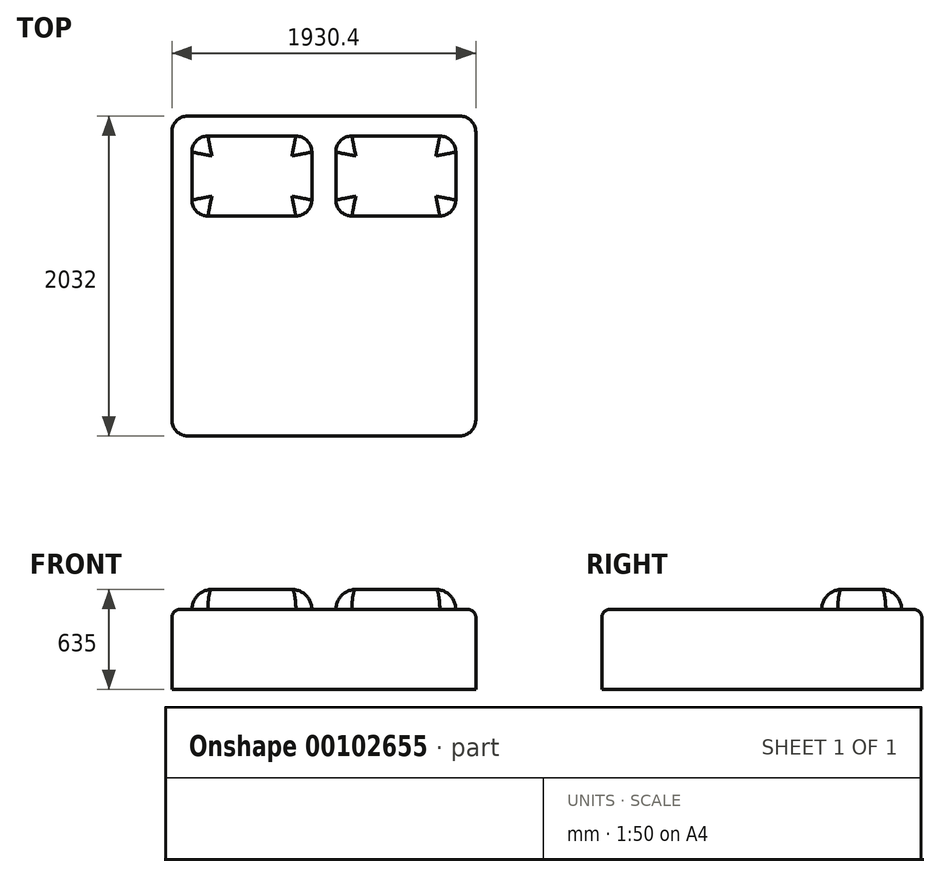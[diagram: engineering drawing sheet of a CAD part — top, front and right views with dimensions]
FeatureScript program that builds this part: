
annotation { "Feature Type Name" : "Feature", "Feature Type Description" : "" }
export const myFeature = defineFeature(function(context is Context, id is Id, definition is map)
    precondition{}
    {
        {
            var Q0;
            Q0=qCreatedBy(makeId("Top.planeOp"),FACE);
            var sketch = newSketch(context, id + "F0", { "sketchPlane" : qUnion([Q0])});
            skLineSegment(sketch, "E0.bottom", {"start": v(0, 0) * mm, "end": v(1930.4, 0) * mm});
            skLineSegment(sketch, "E0.top", {"start": v(0, 2032) * mm, "end": v(1930.4, 2032) * mm});
            skLineSegment(sketch, "E0.left", {"start": v(0, 0) * mm, "end": v(0, 2032) * mm});
            skLineSegment(sketch, "E0.right", {"start": v(1930.4, 0) * mm, "end": v(1930.4, 2032) * mm});
            skSolve(sketch);
        }
        {
            var Q0;
            Q0 = qSketchRegion(id + "F0", true);
            extrude(context, id + "F1", {"entities" : qUnion([Q0]), "depth" : 508 * mm});
        }
        {
            var Q0;
            Q0=makeQuery(id+"F1.opExtrude","CAP_FACE",FACE,{"disambiguationData":[OSD([sQuery(id+"F0.wireOp",EDGE,"E0.bottom"),sQuery(id+"F0.wireOp",EDGE,"E0.top"),sQuery(id+"F0.wireOp",EDGE,"E0.left"),sQuery(id+"F0.wireOp",EDGE,"E0.right")])],"isStart":false});
            var sketch = newSketch(context, id + "F2", { "sketchPlane" : qUnion([Q0])});
            skLineSegment(sketch, "E1.bottom", {"start": v(127, 1905) * mm, "end": v(889, 1905) * mm});
            skLineSegment(sketch, "E1.top", {"start": v(127, 1397) * mm, "end": v(889, 1397) * mm});
            skLineSegment(sketch, "E1.left", {"start": v(127, 1905) * mm, "end": v(127, 1397) * mm});
            skLineSegment(sketch, "E1.right", {"start": v(889, 1905) * mm, "end": v(889, 1397) * mm});
            skLineSegment(sketch, "E2.bottom", {"start": v(1041.4, 1905) * mm, "end": v(1803.4, 1905) * mm});
            skLineSegment(sketch, "E2.top", {"start": v(1041.4, 1397) * mm, "end": v(1803.4, 1397) * mm});
            skLineSegment(sketch, "E2.left", {"start": v(1041.4, 1905) * mm, "end": v(1041.4, 1397) * mm});
            skLineSegment(sketch, "E2.right", {"start": v(1803.4, 1905) * mm, "end": v(1803.4, 1397) * mm});
            skSolve(sketch);
        }
        {
            var Q0;
            Q0 = qSketchRegion(id + "F2", true);
            extrude(context, id + "F3", {"entities" : qUnion([Q0]), "operationType" : NewBodyOperationType.ADD, "depth" : 127 * mm});
        }
        {
            var Q0;
            Q0=makeQuery(id+"F1.opExtrude","SWEPT_EDGE",EDGE,{"disambiguationData":[OSD([sQuery(id+"F0.wireOp",EDGE,"E0.bottom"),sQuery(id+"F0.wireOp",EDGE,"E0.left")])]});
            var Q1;
            Q1=makeQuery(id+"F1.opExtrude","SWEPT_EDGE",EDGE,{"disambiguationData":[OSD([sQuery(id+"F0.wireOp",EDGE,"E0.bottom"),sQuery(id+"F0.wireOp",EDGE,"E0.right")])]});
            var Q2;
            Q2=makeQuery(id+"F1.opExtrude","SWEPT_EDGE",EDGE,{"disambiguationData":[OSD([sQuery(id+"F0.wireOp",EDGE,"E0.top"),sQuery(id+"F0.wireOp",EDGE,"E0.right")])]});
            var Q3;
            Q3=makeQuery(id+"F3.opExtrude","SWEPT_EDGE",EDGE,{"disambiguationData":[OSD([sQuery(id+"F2.wireOp",EDGE,"E2.bottom"),sQuery(id+"F2.wireOp",EDGE,"E2.right")])]});
            var Q4;
            Q4=makeQuery(id+"F3.opExtrude","SWEPT_EDGE",EDGE,{"disambiguationData":[OSD([sQuery(id+"F2.wireOp",EDGE,"E2.top"),sQuery(id+"F2.wireOp",EDGE,"E2.right")])]});
            var Q5;
            Q5=makeQuery(id+"F3.opExtrude","SWEPT_EDGE",EDGE,{"disambiguationData":[OSD([sQuery(id+"F2.wireOp",EDGE,"E2.top"),sQuery(id+"F2.wireOp",EDGE,"E2.left")])]});
            var Q6;
            Q6=makeQuery(id+"F3.opExtrude","SWEPT_EDGE",EDGE,{"disambiguationData":[OSD([sQuery(id+"F2.wireOp",EDGE,"E1.top"),sQuery(id+"F2.wireOp",EDGE,"E1.right")])]});
            var Q7;
            Q7=makeQuery(id+"F3.opExtrude","SWEPT_EDGE",EDGE,{"disambiguationData":[OSD([sQuery(id+"F2.wireOp",EDGE,"E1.bottom"),sQuery(id+"F2.wireOp",EDGE,"E1.right")])]});
            var Q8;
            Q8=makeQuery(id+"F3.opExtrude","SWEPT_EDGE",EDGE,{"disambiguationData":[OSD([sQuery(id+"F2.wireOp",EDGE,"E1.top"),sQuery(id+"F2.wireOp",EDGE,"E1.left")])]});
            var Q9;
            Q9=makeQuery(id+"F1.opExtrude","SWEPT_EDGE",EDGE,{"disambiguationData":[OSD([sQuery(id+"F0.wireOp",EDGE,"E0.top"),sQuery(id+"F0.wireOp",EDGE,"E0.left")])]});
            var Q10;
            Q10=makeQuery(id+"F3.opExtrude","SWEPT_EDGE",EDGE,{"disambiguationData":[OSD([sQuery(id+"F2.wireOp",EDGE,"E1.bottom"),sQuery(id+"F2.wireOp",EDGE,"E1.left")])]});
            var Q11;
            Q11=makeQuery(id+"F3.opExtrude","SWEPT_EDGE",EDGE,{"disambiguationData":[OSD([sQuery(id+"F2.wireOp",EDGE,"E2.bottom"),sQuery(id+"F2.wireOp",EDGE,"E2.left")])]});
            fillet(context, id + "F4", {"entities" : qUnion([Q0, Q1, Q2, Q3, Q4, Q5, Q6, Q7, Q8, Q9, Q10, Q11]), "radius" : 101.6 * mm, "tangentPropagation" : true, "allowEdgeOverflow" : false});
        }
        {
            var Q0;
            Q0=makeQuery(id+"F1.opExtrude","CAP_EDGE",EDGE,{"disambiguationData":[OSD([sQuery(id+"F0.wireOp",EDGE,"E0.left")])],"isStart":false});
            var Q1;
            {var subQ0=sQuery(id+"F0.wireOp",EDGE,"E0.left");var subQ1=sQuery(id+"F0.wireOp",EDGE,"E0.top");Q1=makeQuery(id+"F4.opFillet","BLEND_EDGE",EDGE,{"blendedFrom":[makeQuery(id+"F1.opExtrude","SWEPT_EDGE",EDGE,{"disambiguationData":[OSD([subQ1,subQ0])]}),makeQuery(id+"F1.opExtrude","CAP_FACE",FACE,{"disambiguationData":[OSD([sQuery(id+"F0.wireOp",EDGE,"E0.bottom"),subQ1,subQ0,sQuery(id+"F0.wireOp",EDGE,"E0.right")])],"isStart":false})],"blendedInto":[makeQuery(id+"F1.opExtrude","CAP_FACE",FACE,{"disambiguationData":[OSD([sQuery(id+"F0.wireOp",EDGE,"E0.bottom"),subQ1,subQ0,sQuery(id+"F0.wireOp",EDGE,"E0.right")])],"isStart":false})]});}
            var Q2;
            {var subQ0=sQuery(id+"F0.wireOp",EDGE,"E0.right");var subQ1=sQuery(id+"F0.wireOp",EDGE,"E0.top");Q2=makeQuery(id+"F4.opFillet","BLEND_EDGE",EDGE,{"blendedFrom":[makeQuery(id+"F1.opExtrude","SWEPT_EDGE",EDGE,{"disambiguationData":[OSD([subQ1,subQ0])]}),makeQuery(id+"F1.opExtrude","CAP_FACE",FACE,{"disambiguationData":[OSD([sQuery(id+"F0.wireOp",EDGE,"E0.bottom"),subQ1,sQuery(id+"F0.wireOp",EDGE,"E0.left"),subQ0])],"isStart":false})],"blendedInto":[makeQuery(id+"F1.opExtrude","CAP_FACE",FACE,{"disambiguationData":[OSD([sQuery(id+"F0.wireOp",EDGE,"E0.bottom"),subQ1,sQuery(id+"F0.wireOp",EDGE,"E0.left"),subQ0])],"isStart":false})]});}
            var Q3;
            Q3=makeQuery(id+"F1.opExtrude","CAP_EDGE",EDGE,{"disambiguationData":[OSD([sQuery(id+"F0.wireOp",EDGE,"E0.right")])],"isStart":false});
            var Q4;
            {var subQ0=sQuery(id+"F0.wireOp",EDGE,"E0.right");var subQ1=sQuery(id+"F0.wireOp",EDGE,"E0.bottom");Q4=makeQuery(id+"F4.opFillet","BLEND_EDGE",EDGE,{"blendedFrom":[makeQuery(id+"F1.opExtrude","SWEPT_EDGE",EDGE,{"disambiguationData":[OSD([subQ1,subQ0])]}),makeQuery(id+"F1.opExtrude","CAP_FACE",FACE,{"disambiguationData":[OSD([subQ1,sQuery(id+"F0.wireOp",EDGE,"E0.top"),sQuery(id+"F0.wireOp",EDGE,"E0.left"),subQ0])],"isStart":false})],"blendedInto":[makeQuery(id+"F1.opExtrude","CAP_FACE",FACE,{"disambiguationData":[OSD([subQ1,sQuery(id+"F0.wireOp",EDGE,"E0.top"),sQuery(id+"F0.wireOp",EDGE,"E0.left"),subQ0])],"isStart":false})]});}
            var Q5;
            Q5=makeQuery(id+"F1.opExtrude","CAP_EDGE",EDGE,{"disambiguationData":[OSD([sQuery(id+"F0.wireOp",EDGE,"E0.bottom")])],"isStart":false});
            var Q6;
            {var subQ0=sQuery(id+"F0.wireOp",EDGE,"E0.left");var subQ1=sQuery(id+"F0.wireOp",EDGE,"E0.bottom");Q6=makeQuery(id+"F4.opFillet","BLEND_EDGE",EDGE,{"blendedFrom":[makeQuery(id+"F1.opExtrude","SWEPT_EDGE",EDGE,{"disambiguationData":[OSD([subQ1,subQ0])]}),makeQuery(id+"F1.opExtrude","CAP_FACE",FACE,{"disambiguationData":[OSD([subQ1,sQuery(id+"F0.wireOp",EDGE,"E0.top"),subQ0,sQuery(id+"F0.wireOp",EDGE,"E0.right")])],"isStart":false})],"blendedInto":[makeQuery(id+"F1.opExtrude","CAP_FACE",FACE,{"disambiguationData":[OSD([subQ1,sQuery(id+"F0.wireOp",EDGE,"E0.top"),subQ0,sQuery(id+"F0.wireOp",EDGE,"E0.right")])],"isStart":false})]});}
            var Q7;
            Q7=makeQuery(id+"F1.opExtrude","CAP_EDGE",EDGE,{"disambiguationData":[OSD([sQuery(id+"F0.wireOp",EDGE,"E0.top")])],"isStart":false});
            fillet(context, id + "F5", {"entities" : qUnion([Q0, Q1, Q2, Q3, Q4, Q5, Q6, Q7]), "radius" : 50.8 * mm, "tangentPropagation" : true, "allowEdgeOverflow" : false});
        }
        {
            var Q0;
            {var subQ0=sQuery(id+"F2.wireOp",EDGE,"E1.left");var subQ1=sQuery(id+"F2.wireOp",EDGE,"E1.top");Q0=makeQuery(id+"F4.opFillet","BLEND_EDGE",EDGE,{"blendedFrom":[makeQuery(id+"F3.opExtrude","SWEPT_EDGE",EDGE,{"disambiguationData":[OSD([subQ1,subQ0])]}),makeQuery(id+"F3.opExtrude","CAP_FACE",FACE,{"disambiguationData":[OSD([sQuery(id+"F2.wireOp",EDGE,"E1.bottom"),subQ1,subQ0,sQuery(id+"F2.wireOp",EDGE,"E1.right")])],"isStart":false})],"blendedInto":[makeQuery(id+"F3.opExtrude","CAP_FACE",FACE,{"disambiguationData":[OSD([sQuery(id+"F2.wireOp",EDGE,"E1.bottom"),subQ1,subQ0,sQuery(id+"F2.wireOp",EDGE,"E1.right")])],"isStart":false})]});}
            var Q1;
            Q1=makeQuery(id+"F3.opExtrude","CAP_EDGE",EDGE,{"disambiguationData":[OSD([sQuery(id+"F2.wireOp",EDGE,"E1.left")])],"isStart":false});
            var Q2;
            {var subQ0=sQuery(id+"F2.wireOp",EDGE,"E1.left");var subQ1=sQuery(id+"F2.wireOp",EDGE,"E1.bottom");Q2=makeQuery(id+"F4.opFillet","BLEND_EDGE",EDGE,{"blendedFrom":[makeQuery(id+"F3.opExtrude","SWEPT_EDGE",EDGE,{"disambiguationData":[OSD([subQ1,subQ0])]}),makeQuery(id+"F3.opExtrude","CAP_FACE",FACE,{"disambiguationData":[OSD([subQ1,sQuery(id+"F2.wireOp",EDGE,"E1.top"),subQ0,sQuery(id+"F2.wireOp",EDGE,"E1.right")])],"isStart":false})],"blendedInto":[makeQuery(id+"F3.opExtrude","CAP_FACE",FACE,{"disambiguationData":[OSD([subQ1,sQuery(id+"F2.wireOp",EDGE,"E1.top"),subQ0,sQuery(id+"F2.wireOp",EDGE,"E1.right")])],"isStart":false})]});}
            var Q3;
            Q3=makeQuery(id+"F3.opExtrude","CAP_EDGE",EDGE,{"disambiguationData":[OSD([sQuery(id+"F2.wireOp",EDGE,"E1.bottom")])],"isStart":false});
            var Q4;
            {var subQ0=sQuery(id+"F2.wireOp",EDGE,"E1.right");var subQ1=sQuery(id+"F2.wireOp",EDGE,"E1.bottom");Q4=makeQuery(id+"F4.opFillet","BLEND_EDGE",EDGE,{"blendedFrom":[makeQuery(id+"F3.opExtrude","SWEPT_EDGE",EDGE,{"disambiguationData":[OSD([subQ1,subQ0])]}),makeQuery(id+"F3.opExtrude","CAP_FACE",FACE,{"disambiguationData":[OSD([subQ1,sQuery(id+"F2.wireOp",EDGE,"E1.top"),sQuery(id+"F2.wireOp",EDGE,"E1.left"),subQ0])],"isStart":false})],"blendedInto":[makeQuery(id+"F3.opExtrude","CAP_FACE",FACE,{"disambiguationData":[OSD([subQ1,sQuery(id+"F2.wireOp",EDGE,"E1.top"),sQuery(id+"F2.wireOp",EDGE,"E1.left"),subQ0])],"isStart":false})]});}
            var Q5;
            {var subQ0=sQuery(id+"F2.wireOp",EDGE,"E1.right");var subQ1=sQuery(id+"F2.wireOp",EDGE,"E1.top");Q5=makeQuery(id+"F4.opFillet","BLEND_EDGE",EDGE,{"blendedFrom":[makeQuery(id+"F3.opExtrude","SWEPT_EDGE",EDGE,{"disambiguationData":[OSD([subQ1,subQ0])]}),makeQuery(id+"F3.opExtrude","CAP_FACE",FACE,{"disambiguationData":[OSD([sQuery(id+"F2.wireOp",EDGE,"E1.bottom"),subQ1,sQuery(id+"F2.wireOp",EDGE,"E1.left"),subQ0])],"isStart":false})],"blendedInto":[makeQuery(id+"F3.opExtrude","CAP_FACE",FACE,{"disambiguationData":[OSD([sQuery(id+"F2.wireOp",EDGE,"E1.bottom"),subQ1,sQuery(id+"F2.wireOp",EDGE,"E1.left"),subQ0])],"isStart":false})]});}
            var Q6;
            Q6=makeQuery(id+"F3.opExtrude","CAP_EDGE",EDGE,{"disambiguationData":[OSD([sQuery(id+"F2.wireOp",EDGE,"E1.right")])],"isStart":false});
            var Q7;
            Q7=makeQuery(id+"F3.opExtrude","CAP_EDGE",EDGE,{"disambiguationData":[OSD([sQuery(id+"F2.wireOp",EDGE,"E1.top")])],"isStart":false});
            var Q8;
            {var subQ0=sQuery(id+"F2.wireOp",EDGE,"E2.left");var subQ1=sQuery(id+"F2.wireOp",EDGE,"E2.bottom");Q8=makeQuery(id+"F4.opFillet","BLEND_EDGE",EDGE,{"blendedFrom":[makeQuery(id+"F3.opExtrude","SWEPT_EDGE",EDGE,{"disambiguationData":[OSD([subQ1,subQ0])]}),makeQuery(id+"F3.opExtrude","CAP_FACE",FACE,{"disambiguationData":[OSD([subQ1,sQuery(id+"F2.wireOp",EDGE,"E2.top"),subQ0,sQuery(id+"F2.wireOp",EDGE,"E2.right")])],"isStart":false})],"blendedInto":[makeQuery(id+"F3.opExtrude","CAP_FACE",FACE,{"disambiguationData":[OSD([subQ1,sQuery(id+"F2.wireOp",EDGE,"E2.top"),subQ0,sQuery(id+"F2.wireOp",EDGE,"E2.right")])],"isStart":false})]});}
            var Q9;
            Q9=makeQuery(id+"F3.opExtrude","CAP_EDGE",EDGE,{"disambiguationData":[OSD([sQuery(id+"F2.wireOp",EDGE,"E2.left")])],"isStart":false});
            var Q10;
            {var subQ0=sQuery(id+"F2.wireOp",EDGE,"E2.left");var subQ1=sQuery(id+"F2.wireOp",EDGE,"E2.top");Q10=makeQuery(id+"F4.opFillet","BLEND_EDGE",EDGE,{"blendedFrom":[makeQuery(id+"F3.opExtrude","SWEPT_EDGE",EDGE,{"disambiguationData":[OSD([subQ1,subQ0])]}),makeQuery(id+"F3.opExtrude","CAP_FACE",FACE,{"disambiguationData":[OSD([sQuery(id+"F2.wireOp",EDGE,"E2.bottom"),subQ1,subQ0,sQuery(id+"F2.wireOp",EDGE,"E2.right")])],"isStart":false})],"blendedInto":[makeQuery(id+"F3.opExtrude","CAP_FACE",FACE,{"disambiguationData":[OSD([sQuery(id+"F2.wireOp",EDGE,"E2.bottom"),subQ1,subQ0,sQuery(id+"F2.wireOp",EDGE,"E2.right")])],"isStart":false})]});}
            var Q11;
            Q11=makeQuery(id+"F3.opExtrude","CAP_EDGE",EDGE,{"disambiguationData":[OSD([sQuery(id+"F2.wireOp",EDGE,"E2.top")])],"isStart":false});
            var Q12;
            Q12=makeQuery(id+"F3.opExtrude","CAP_EDGE",EDGE,{"disambiguationData":[OSD([sQuery(id+"F2.wireOp",EDGE,"E2.right")])],"isStart":false});
            var Q13;
            {var subQ0=sQuery(id+"F2.wireOp",EDGE,"E2.right");var subQ1=sQuery(id+"F2.wireOp",EDGE,"E2.top");Q13=makeQuery(id+"F4.opFillet","BLEND_EDGE",EDGE,{"blendedFrom":[makeQuery(id+"F3.opExtrude","SWEPT_EDGE",EDGE,{"disambiguationData":[OSD([subQ1,subQ0])]}),makeQuery(id+"F3.opExtrude","CAP_FACE",FACE,{"disambiguationData":[OSD([sQuery(id+"F2.wireOp",EDGE,"E2.bottom"),subQ1,sQuery(id+"F2.wireOp",EDGE,"E2.left"),subQ0])],"isStart":false})],"blendedInto":[makeQuery(id+"F3.opExtrude","CAP_FACE",FACE,{"disambiguationData":[OSD([sQuery(id+"F2.wireOp",EDGE,"E2.bottom"),subQ1,sQuery(id+"F2.wireOp",EDGE,"E2.left"),subQ0])],"isStart":false})]});}
            var Q14;
            {var subQ0=sQuery(id+"F2.wireOp",EDGE,"E2.right");var subQ1=sQuery(id+"F2.wireOp",EDGE,"E2.bottom");Q14=makeQuery(id+"F4.opFillet","BLEND_EDGE",EDGE,{"blendedFrom":[makeQuery(id+"F3.opExtrude","SWEPT_EDGE",EDGE,{"disambiguationData":[OSD([subQ1,subQ0])]}),makeQuery(id+"F3.opExtrude","CAP_FACE",FACE,{"disambiguationData":[OSD([subQ1,sQuery(id+"F2.wireOp",EDGE,"E2.top"),sQuery(id+"F2.wireOp",EDGE,"E2.left"),subQ0])],"isStart":false})],"blendedInto":[makeQuery(id+"F3.opExtrude","CAP_FACE",FACE,{"disambiguationData":[OSD([subQ1,sQuery(id+"F2.wireOp",EDGE,"E2.top"),sQuery(id+"F2.wireOp",EDGE,"E2.left"),subQ0])],"isStart":false})]});}
            var Q15;
            Q15=makeQuery(id+"F3.opExtrude","CAP_EDGE",EDGE,{"disambiguationData":[OSD([sQuery(id+"F2.wireOp",EDGE,"E2.bottom")])],"isStart":false});
            fillet(context, id + "F6", {"entities" : qUnion([Q0, Q1, Q2, Q3, Q4, Q5, Q6, Q7, Q8, Q9, Q10, Q11, Q12, Q13, Q14, Q15]), "radius" : 127 * mm, "tangentPropagation" : true, "allowEdgeOverflow" : false});
        }
    });
